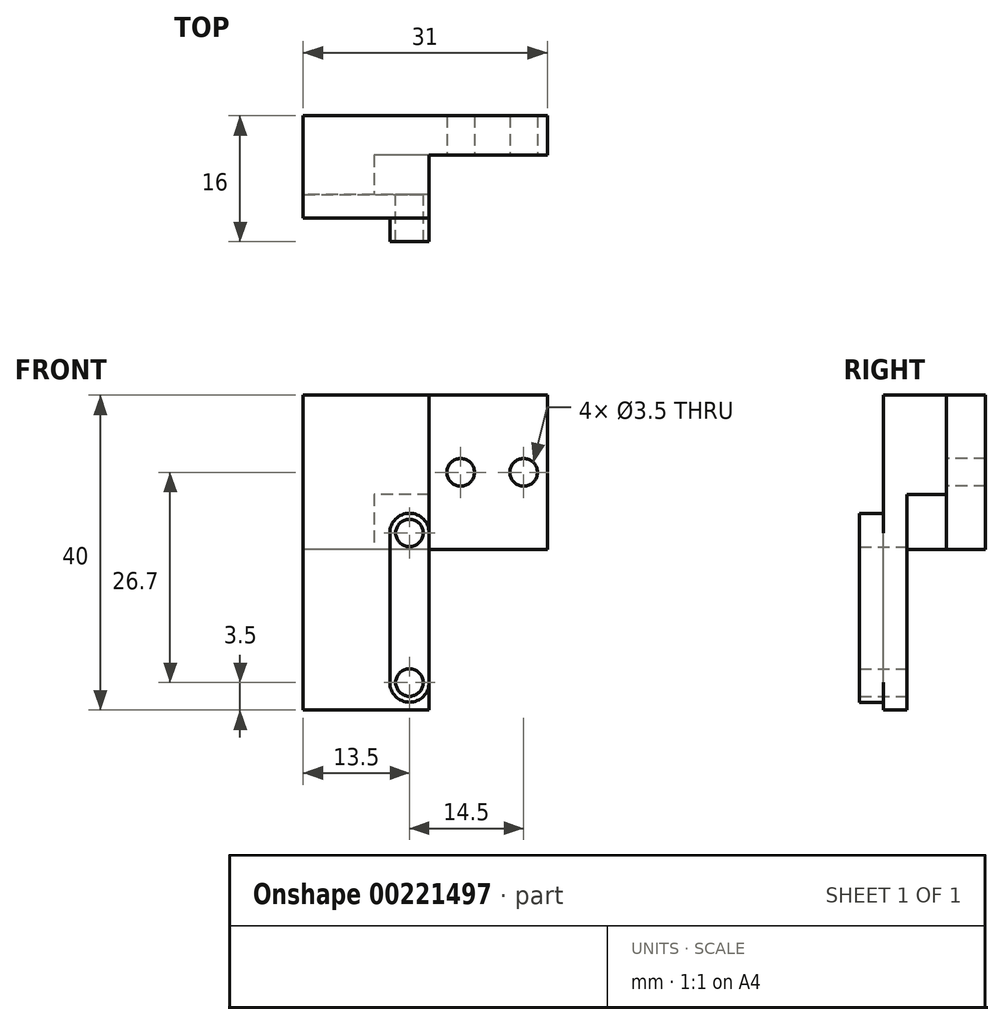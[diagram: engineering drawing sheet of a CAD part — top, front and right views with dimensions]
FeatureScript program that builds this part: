
annotation { "Feature Type Name" : "Feature", "Feature Type Description" : "" }
export const myFeature = defineFeature(function(context is Context, id is Id, definition is map)
    precondition{}
    {
        {
            var Q0;
            Q0=qCreatedBy(makeId("Front.planeOp"),FACE);
            var sketch = newSketch(context, id + "F0", { "sketchPlane" : qUnion([Q0])});
            skLineSegment(sketch, "E0.bottom", {"start": v(0, 0) * mm, "end": v(16, 0) * mm});
            skLineSegment(sketch, "E0.top", {"start": v(0, 40) * mm, "end": v(16, 40) * mm});
            skLineSegment(sketch, "E0.left", {"start": v(0, 0) * mm, "end": v(0, 40) * mm});
            skLineSegment(sketch, "E0.right", {"start": v(16, 0) * mm, "end": v(16, 40) * mm});
            skCircle(sketch, "E1", {"center": v(13.5, 3.5) * mm, "radius": 1.75 * mm});
            skCircle(sketch, "E2", {"center": v(13.5, 22.5) * mm, "radius": 1.75 * mm});
            skSolve(sketch);
        }
        {
            var Q0;
            Q0=makeQuery(id+"F0.imprint","IMPRINT",FACE,{"disambiguationData":[TD([[makeQuery(id+"F0.imprint","IMPRINT",EDGE,{"derivedFrom":sQuery(id+"F0.wireOp",EDGE,"E0.bottom")}),1.0]])]});
            extrude(context, id + "F1", {"entities" : qUnion([Q0]), "depth" : 3 * mm});
        }
        {
            var Q0;
            Q0=makeQuery(id+"F1.opExtrude","CAP_FACE",FACE,{"disambiguationData":[OSD([sQuery(id+"F0.wireOp",EDGE,"E0.bottom"),sQuery(id+"F0.wireOp",EDGE,"E0.top"),sQuery(id+"F0.wireOp",EDGE,"E0.left"),sQuery(id+"F0.wireOp",EDGE,"E0.right"),sQuery(id+"F0.wireOp",EDGE,"E1"),sQuery(id+"F0.wireOp",EDGE,"E2")])],"isStart":false});
            var sketch = newSketch(context, id + "F2", { "sketchPlane" : qUnion([Q0])});
            skCircle(sketch, "E3", {"center": v(13.5, 22.5) * mm, "radius": 1.75 * mm});
            skCircle(sketch, "E4", {"center": v(13.5, 3.5) * mm, "radius": 1.75 * mm});
            skLineSegment(sketch, "E5", {"start": v(13.5, 3.5) * mm, "end": v(13.5, 22.5) * mm, "construction": true});
            skArc(sketch, "E6.0.startCap", {"start": v(16, 3.5) * mm, "mid": v(13.5, 1) * mm, "end": v(11, 3.5) * mm});
            skArc(sketch, "E6.0.endCap", {"start": v(11, 22.5) * mm, "mid": v(13.5, 25) * mm, "end": v(16, 22.5) * mm});
            skLineSegment(sketch, "E6.0.left", {"start": v(11, 3.5) * mm, "end": v(11, 22.5) * mm});
            skLineSegment(sketch, "E6.0.right", {"start": v(16, 3.5) * mm, "end": v(16, 22.5) * mm});
            skSolve(sketch);
        }
        {
            var Q0;
            Q0=makeQuery(id+"F2.imprint","IMPRINT",FACE,{"disambiguationData":[TD([[makeQuery(id+"F2.imprint","IMPRINT",EDGE,{"derivedFrom":sQuery(id+"F2.wireOp",EDGE,"E3")}),-1.0]])]});
            extrude(context, id + "F3", {"entities" : qUnion([Q0]), "operationType" : NewBodyOperationType.ADD, "depth" : 3 * mm});
        }
        {
            var Q0;
            Q0=makeQuery(id+"F1.opExtrude","CAP_FACE",FACE,{"disambiguationData":[OSD([sQuery(id+"F0.wireOp",EDGE,"E0.bottom"),sQuery(id+"F0.wireOp",EDGE,"E0.top"),sQuery(id+"F0.wireOp",EDGE,"E0.left"),sQuery(id+"F0.wireOp",EDGE,"E0.right"),sQuery(id+"F0.wireOp",EDGE,"E1"),sQuery(id+"F0.wireOp",EDGE,"E2")])],"isStart":true});
            var sketch = newSketch(context, id + "F4", { "sketchPlane" : qUnion([Q0])});
            skLineSegment(sketch, "E7.bottom", {"start": v(-16, 40) * mm, "end": v(0, 40) * mm});
            skLineSegment(sketch, "E7.top", {"start": v(-16, 20.4) * mm, "end": v(0, 20.4) * mm});
            skLineSegment(sketch, "E7.left", {"start": v(-16, 40) * mm, "end": v(-16, 20.4) * mm});
            skLineSegment(sketch, "E7.right", {"start": v(0, 40) * mm, "end": v(0, 20.4) * mm});
            skSolve(sketch);
        }
        {
            var Q0;
            Q0=makeQuery(id+"F4.imprint","IMPRINT",FACE,{"disambiguationData":[TD([[makeQuery(id+"F4.imprint","IMPRINT",EDGE,{"derivedFrom":sQuery(id+"F4.wireOp",EDGE,"E7.bottom")}),1.0]])]});
            extrude(context, id + "F5", {"entities" : qUnion([Q0]), "operationType" : NewBodyOperationType.ADD, "depth" : 10 * mm});
        }
        {
            var Q0;
            Q0=makeQuery(id+"F5.boolean.opBoolean","MERGE",FACE,{"derivedFrom":[makeQuery(id+"F3.boolean.opBoolean","MERGE",FACE,{"derivedFrom":[makeQuery(id+"F1.opExtrude","SWEPT_FACE",FACE,{"disambiguationData":[OSD([sQuery(id+"F0.wireOp",EDGE,"E0.right")])]}),makeQuery(id+"F3.opExtrude","SWEPT_FACE",FACE,{"disambiguationData":[OSD([sQuery(id+"F2.wireOp",EDGE,"E6.0.right")])]})]}),makeQuery(id+"F5.opExtrude","SWEPT_FACE",FACE,{"disambiguationData":[OSD([sQuery(id+"F4.wireOp",EDGE,"E7.left")])]})]});
            var sketch = newSketch(context, id + "F6", { "sketchPlane" : qUnion([Q0])});
            skLineSegment(sketch, "E8.bottom", {"start": v(10, 20.4) * mm, "end": v(5, 20.4) * mm});
            skLineSegment(sketch, "E8.top", {"start": v(10, 40) * mm, "end": v(5, 40) * mm});
            skLineSegment(sketch, "E8.left", {"start": v(10, 20.4) * mm, "end": v(10, 40) * mm});
            skLineSegment(sketch, "E8.right", {"start": v(5, 20.4) * mm, "end": v(5, 40) * mm});
            skSolve(sketch);
        }
        {
            var Q0;
            Q0=makeQuery(id+"F6.imprint","IMPRINT",FACE,{"disambiguationData":[TD([[makeQuery(id+"F6.imprint","IMPRINT",EDGE,{"derivedFrom":sQuery(id+"F6.wireOp",EDGE,"E8.bottom")}),-1.0]])]});
            extrude(context, id + "F7", {"entities" : qUnion([Q0]), "operationType" : NewBodyOperationType.ADD, "depth" : 15 * mm});
        }
        {
            var Q0;
            Q0=makeQuery(id+"F7.opExtrude","SWEPT_FACE",FACE,{"disambiguationData":[OSD([sQuery(id+"F6.wireOp",EDGE,"E8.right")])]});
            var sketch = newSketch(context, id + "F8", { "sketchPlane" : qUnion([Q0])});
            skCircle(sketch, "E9", {"center": v(28, 30.2) * mm, "radius": 1.75 * mm});
            skPoint(sketch, "E9.centerSnap0", {"position": v(31, 30.2) * mm});
            skCircle(sketch, "E10", {"center": v(20, 30.2) * mm, "radius": 1.75 * mm});
            skSolve(sketch);
        }
        {
            var Q0;
            Q0=makeQuery(id+"F8.imprint","IMPRINT",FACE,{"disambiguationData":[TD([[makeQuery(id+"F8.imprint","IMPRINT",EDGE,{"derivedFrom":sQuery(id+"F8.wireOp",EDGE,"E10")}),1.0]])]});
            var Q1;
            Q1=makeQuery(id+"F8.imprint","IMPRINT",FACE,{"disambiguationData":[TD([[makeQuery(id+"F8.imprint","IMPRINT",EDGE,{"derivedFrom":sQuery(id+"F8.wireOp",EDGE,"E9")}),1.0]])]});
            var Q2;
            Q2=makeQuery(id+"F7.boolean.opBoolean","MERGE",FACE,{"derivedFrom":[makeQuery(id+"F5.opExtrude","CAP_FACE",FACE,{"disambiguationData":[OSD([sQuery(id+"F4.wireOp",EDGE,"E7.bottom"),sQuery(id+"F4.wireOp",EDGE,"E7.top"),sQuery(id+"F4.wireOp",EDGE,"E7.left"),sQuery(id+"F4.wireOp",EDGE,"E7.right")])],"isStart":false}),makeQuery(id+"F7.opExtrude","SWEPT_FACE",FACE,{"disambiguationData":[OSD([sQuery(id+"F6.wireOp",EDGE,"E8.left")])]})]});
            extrude(context, id + "F9", {"entities" : qUnion([Q0, Q1]), "operationType" : NewBodyOperationType.REMOVE, "endBound" : BoundingType.UP_TO_SURFACE, "oppositeDirection" : true, "endBoundEntityFace" : qUnion([Q2]), "depth" : 25 * mm});
        }
        {
            var Q0;
            Q0=makeQuery(id+"F7.boolean.opBoolean","MERGE",FACE,{"derivedFrom":[makeQuery(id+"F5.opExtrude","SWEPT_FACE",FACE,{"disambiguationData":[OSD([sQuery(id+"F4.wireOp",EDGE,"E7.top")])]}),makeQuery(id+"F7.opExtrude","SWEPT_FACE",FACE,{"disambiguationData":[OSD([sQuery(id+"F6.wireOp",EDGE,"E8.bottom")])]})]});
            var sketch = newSketch(context, id + "F10", { "sketchPlane" : qUnion([Q0])});
            skLineSegment(sketch, "E11.bottom", {"start": v(16, -5) * mm, "end": v(9, -5) * mm});
            skLineSegment(sketch, "E11.top", {"start": v(16, 0) * mm, "end": v(9, 0) * mm});
            skLineSegment(sketch, "E11.left", {"start": v(16, -5) * mm, "end": v(16, 0) * mm});
            skLineSegment(sketch, "E11.right", {"start": v(9, -5) * mm, "end": v(9, 0) * mm});
            skSolve(sketch);
        }
        {
            var Q0;
            Q0=makeQuery(id+"F10.imprint","IMPRINT",FACE,{"disambiguationData":[TD([[makeQuery(id+"F10.imprint","IMPRINT",EDGE,{"derivedFrom":sQuery(id+"F10.wireOp",EDGE,"E11.bottom")}),-1.0]])]});
            extrude(context, id + "F11", {"entities" : qUnion([Q0]), "operationType" : NewBodyOperationType.REMOVE, "oppositeDirection" : true, "depth" : 7 * mm});
        }
        {
            var Q0;
            Q0=makeQuery(id+"F11.boolean.opBoolean","MERGE",FACE,{"derivedFrom":[makeQuery(id+"F7.opExtrude","SWEPT_FACE",FACE,{"disambiguationData":[OSD([sQuery(id+"F6.wireOp",EDGE,"E8.right")])]}),makeQuery(id+"F11.opExtrude","SWEPT_FACE",FACE,{"disambiguationData":[OSD([sQuery(id+"F10.wireOp",EDGE,"E11.bottom")])]})]});
            var sketch = newSketch(context, id + "F12", { "sketchPlane" : qUnion([Q0])});
            skCircle(sketch, "E12", {"center": v(13.5, 22.5) * mm, "radius": 1.75 * mm});
            skSolve(sketch);
        }
        {
            var Q0;
            Q0=makeQuery(id+"F12.imprint","IMPRINT",FACE,{"disambiguationData":[TD([[makeQuery(id+"F12.imprint","IMPRINT",EDGE,{"derivedFrom":sQuery(id+"F12.wireOp",EDGE,"E12")}),1.0]])]});
            var Q1;
            Q1=makeQuery(id+"F7.boolean.opBoolean","MERGE",FACE,{"derivedFrom":[makeQuery(id+"F5.opExtrude","CAP_FACE",FACE,{"disambiguationData":[OSD([sQuery(id+"F0.wireOp",EDGE,"E2"),sQuery(id+"F4.wireOp",EDGE,"E7.bottom"),sQuery(id+"F4.wireOp",EDGE,"E7.top"),sQuery(id+"F4.wireOp",EDGE,"E7.left"),sQuery(id+"F4.wireOp",EDGE,"E7.right")])],"isStart":false}),makeQuery(id+"F7.opExtrude","SWEPT_FACE",FACE,{"disambiguationData":[OSD([sQuery(id+"F6.wireOp",EDGE,"E8.left")])]})]});
            extrude(context, id + "F13", {"entities" : qUnion([Q0]), "operationType" : NewBodyOperationType.ADD, "endBound" : BoundingType.UP_TO_SURFACE, "oppositeDirection" : true, "endBoundEntityFace" : qUnion([Q1]), "depth" : 25 * mm});
        }
    });
